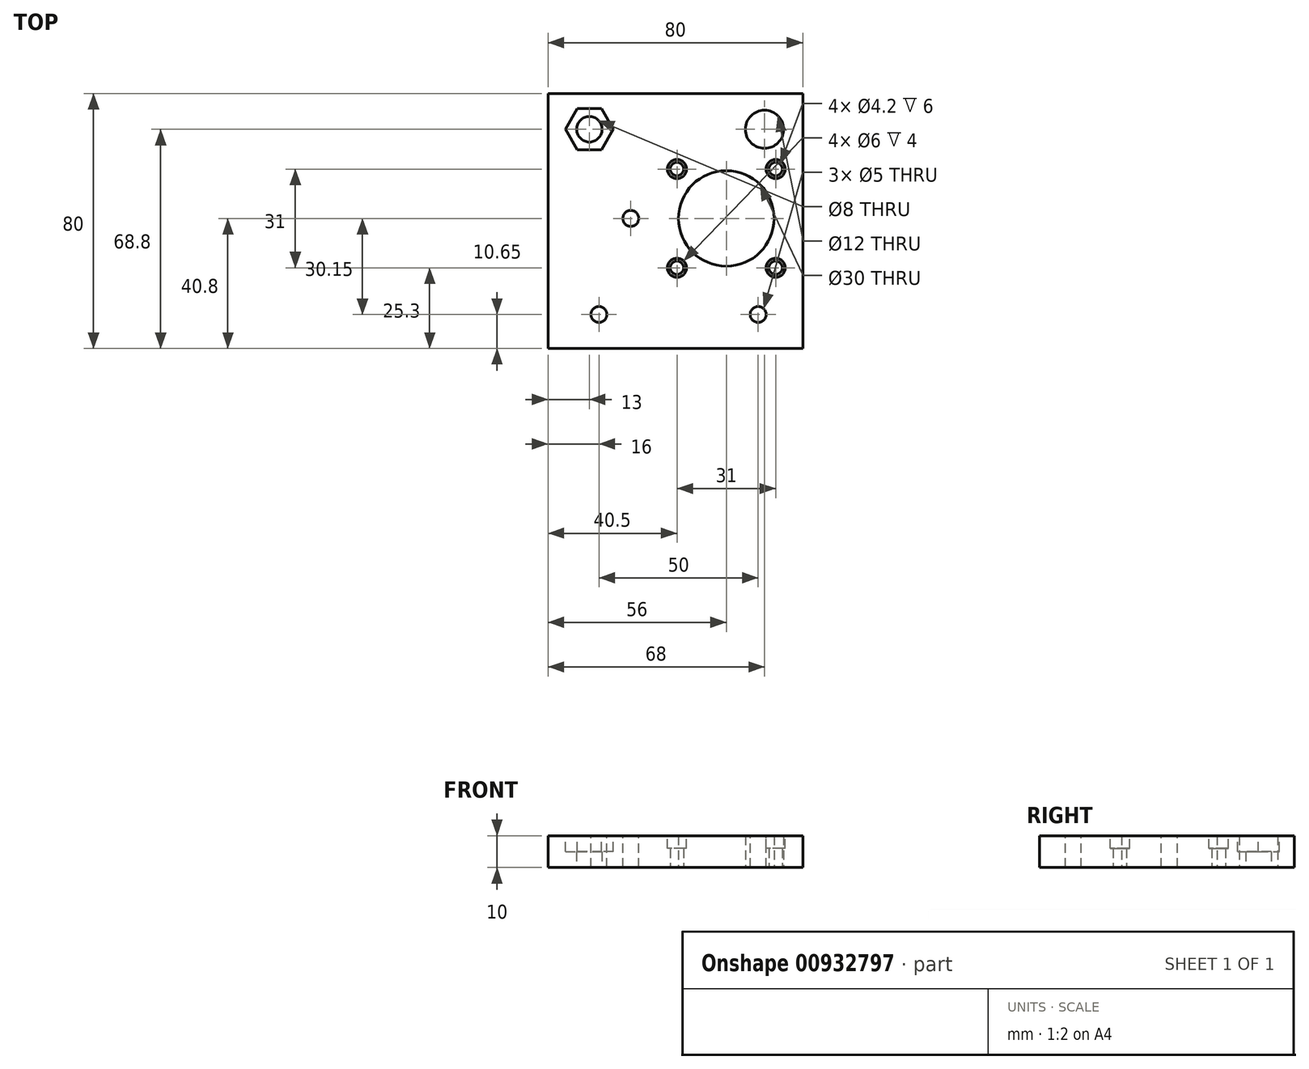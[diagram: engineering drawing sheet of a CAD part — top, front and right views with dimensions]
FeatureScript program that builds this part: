
annotation { "Feature Type Name" : "Feature", "Feature Type Description" : "" }
export const myFeature = defineFeature(function(context is Context, id is Id, definition is map)
    precondition{}
    {
        {
            var Q0;
            Q0=qCreatedBy(makeId("Top.planeOp"),FACE);
            var sketch = newSketch(context, id + "F0", { "sketchPlane" : qUnion([Q0])});
            skLineSegment(sketch, "E0.bottom", {"start": v(0, 0) * mm, "end": v(80, 0) * mm});
            skLineSegment(sketch, "E0.top", {"start": v(0, -80) * mm, "end": v(80, -80) * mm});
            skLineSegment(sketch, "E0.left", {"start": v(0, 0) * mm, "end": v(0, -80) * mm});
            skLineSegment(sketch, "E0.right", {"start": v(80, 0) * mm, "end": v(80, -80) * mm});
            skCircle(sketch, "E1", {"center": v(13, -11.2) * mm, "radius": 4 * mm});
            skCircle(sketch, "E2", {"center": v(68, -11.2) * mm, "radius": 6 * mm});
            skCircle(sketch, "E3", {"center": v(56, -39.2) * mm, "radius": 15 * mm});
            skCircle(sketch, "E4", {"center": v(40.5, -23.7) * mm, "radius": 2.1 * mm});
            skCircle(sketch, "E5", {"center": v(71.5, -23.7) * mm, "radius": 2.1 * mm});
            skCircle(sketch, "E6", {"center": v(71.5, -54.7) * mm, "radius": 2.1 * mm});
            skCircle(sketch, "E7", {"center": v(40.5, -54.7) * mm, "radius": 2.1 * mm});
            skSolve(sketch);
        }
        {
            var Q0;
            Q0=makeQuery(id+"F0.imprint","IMPRINT",FACE,{"disambiguationData":[TD([[makeQuery(id+"F0.imprint","IMPRINT",EDGE,{"derivedFrom":sQuery(id+"F0.wireOp",EDGE,"E0.bottom")}),-1.0]])]});
            extrude(context, id + "F1", {"entities" : qUnion([Q0]), "depth" : 10 * mm, "offsetDistance" : 25 * mm});
        }
        {
            var Q0;
            Q0=makeQuery(id+"F1.opExtrude","CAP_FACE",FACE,{"disambiguationData":[OSD([sQuery(id+"F0.wireOp",EDGE,"E0.bottom"),sQuery(id+"F0.wireOp",EDGE,"E0.top"),sQuery(id+"F0.wireOp",EDGE,"E0.left"),sQuery(id+"F0.wireOp",EDGE,"E0.right"),sQuery(id+"F0.wireOp",EDGE,"E1"),sQuery(id+"F0.wireOp",EDGE,"E2"),sQuery(id+"F0.wireOp",EDGE,"E3"),sQuery(id+"F0.wireOp",EDGE,"E4"),sQuery(id+"F0.wireOp",EDGE,"E5"),sQuery(id+"F0.wireOp",EDGE,"E6"),sQuery(id+"F0.wireOp",EDGE,"E7")])],"isStart":false});
            var sketch = newSketch(context, id + "F2", { "sketchPlane" : qUnion([Q0])});
            skPoint(sketch, "E8", {"position": v(56, -39.2) * mm});
            skCircle(sketch, "E9", {"center": v(26, -39.2) * mm, "radius": 2.5 * mm});
            skCircle(sketch, "E10", {"center": v(16, -69.35) * mm, "radius": 2.5 * mm});
            skCircle(sketch, "E11", {"center": v(66, -69.35) * mm, "radius": 2.5 * mm});
            skSolve(sketch);
        }
        {
            var Q0;
            Q0 = qSketchRegion(id + "F2", true);
            extrude(context, id + "F3", {"entities" : qUnion([Q0]), "operationType" : NewBodyOperationType.REMOVE, "oppositeDirection" : true, "depth" : 25 * mm, "offsetDistance" : 25 * mm});
        }
        {
            var Q0;
            Q0=makeQuery(id+"F1.opExtrude","CAP_FACE",FACE,{"disambiguationData":[OSD([sQuery(id+"F0.wireOp",EDGE,"E0.bottom"),sQuery(id+"F0.wireOp",EDGE,"E0.top"),sQuery(id+"F0.wireOp",EDGE,"E0.left"),sQuery(id+"F0.wireOp",EDGE,"E0.right"),sQuery(id+"F0.wireOp",EDGE,"E1"),sQuery(id+"F0.wireOp",EDGE,"E2"),sQuery(id+"F0.wireOp",EDGE,"E3"),sQuery(id+"F0.wireOp",EDGE,"E4"),sQuery(id+"F0.wireOp",EDGE,"E5"),sQuery(id+"F0.wireOp",EDGE,"E6"),sQuery(id+"F0.wireOp",EDGE,"E7")])],"isStart":false});
            var sketch = newSketch(context, id + "F4", { "sketchPlane" : qUnion([Q0])});
            skCircle(sketch, "E12", {"center": v(40.5, -23.7) * mm, "radius": 3 * mm});
            skCircle(sketch, "E13", {"center": v(71.5, -23.7) * mm, "radius": 3 * mm});
            skCircle(sketch, "E14", {"center": v(40.5, -54.7) * mm, "radius": 3 * mm});
            skCircle(sketch, "E15", {"center": v(71.5, -54.7) * mm, "radius": 3 * mm});
            skSolve(sketch);
        }
        {
            var Q0;
            Q0 = qSketchRegion(id + "F4", true);
            extrude(context, id + "F5", {"entities" : qUnion([Q0]), "operationType" : NewBodyOperationType.REMOVE, "oppositeDirection" : true, "depth" : 4 * mm, "offsetDistance" : 25 * mm});
        }
        {
            var Q0;
            Q0=makeQuery(id+"F1.opExtrude","CAP_FACE",FACE,{"disambiguationData":[OSD([sQuery(id+"F0.wireOp",EDGE,"E0.bottom"),sQuery(id+"F0.wireOp",EDGE,"E0.top"),sQuery(id+"F0.wireOp",EDGE,"E0.left"),sQuery(id+"F0.wireOp",EDGE,"E0.right"),sQuery(id+"F0.wireOp",EDGE,"E1"),sQuery(id+"F0.wireOp",EDGE,"E2"),sQuery(id+"F0.wireOp",EDGE,"E3"),sQuery(id+"F0.wireOp",EDGE,"E4"),sQuery(id+"F0.wireOp",EDGE,"E5"),sQuery(id+"F0.wireOp",EDGE,"E6"),sQuery(id+"F0.wireOp",EDGE,"E7")])],"isStart":false});
            var sketch = newSketch(context, id + "F6", { "sketchPlane" : qUnion([Q0])});
            skLineSegment(sketch, "E16", {"start": v(9.25, -4.7) * mm, "end": v(16.75, -4.7) * mm});
            skLineSegment(sketch, "E17", {"start": v(16.75, -4.7) * mm, "end": v(20.5, -11.2) * mm});
            skLineSegment(sketch, "E18", {"start": v(20.5, -11.2) * mm, "end": v(16.75, -17.7) * mm});
            skLineSegment(sketch, "E19", {"start": v(16.75, -17.7) * mm, "end": v(9.25, -17.7) * mm});
            skLineSegment(sketch, "E20", {"start": v(9.25, -17.7) * mm, "end": v(5.5, -11.2) * mm});
            skLineSegment(sketch, "E21", {"start": v(5.5, -11.2) * mm, "end": v(9.25, -4.7) * mm});
            skPoint(sketch, "E22", {"position": v(13, -11.2) * mm});
            skSolve(sketch);
        }
        {
            var Q0;
            Q0 = qSketchRegion(id + "F6", true);
            extrude(context, id + "F7", {"entities" : qUnion([Q0]), "operationType" : NewBodyOperationType.REMOVE, "oppositeDirection" : true, "depth" : 5 * mm, "offsetDistance" : 25 * mm});
        }
    });
